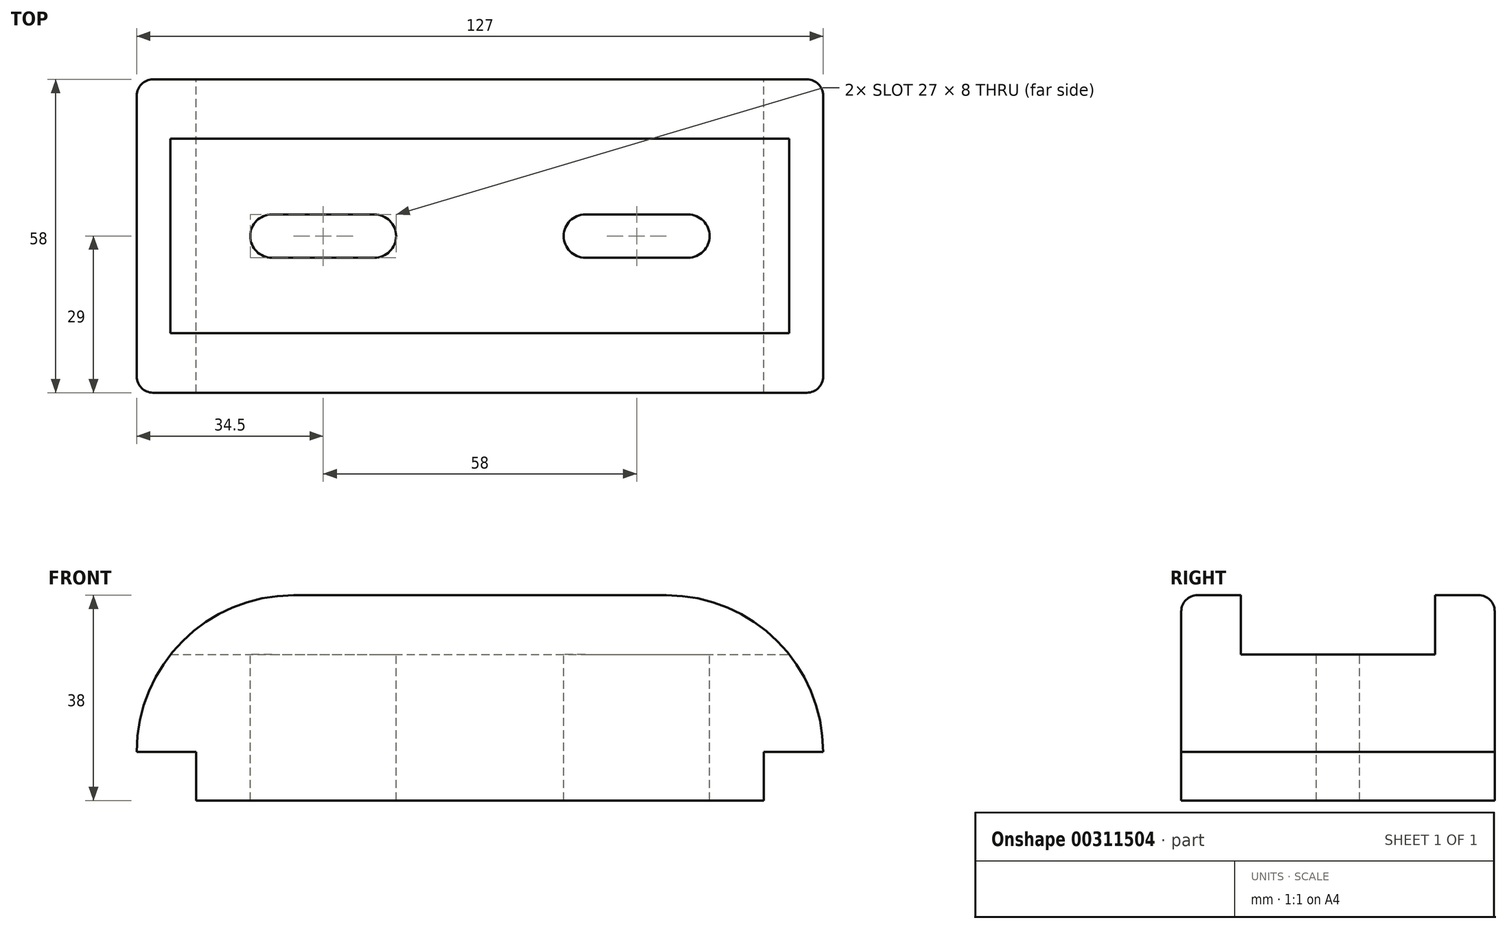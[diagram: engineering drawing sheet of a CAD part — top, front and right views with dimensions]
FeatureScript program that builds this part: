
annotation { "Feature Type Name" : "Feature", "Feature Type Description" : "" }
export const myFeature = defineFeature(function(context is Context, id is Id, definition is map)
    precondition{}
    {
        {
            var Q0;
            Q0=qCreatedBy(makeId("Front.planeOp"),FACE);
            var sketch = newSketch(context, id + "F0", { "sketchPlane" : qUnion([Q0])});
            skLineSegment(sketch, "E0", {"start": v(0, 0) * mm, "end": v(0, 9) * mm});
            skLineSegment(sketch, "E1", {"start": v(0, 9) * mm, "end": v(-11, 9) * mm});
            skLineSegment(sketch, "E2", {"start": v(0, 0) * mm, "end": v(105, 0) * mm});
            skLineSegment(sketch, "E3", {"start": v(105, 0) * mm, "end": v(105, 9) * mm});
            skLineSegment(sketch, "E4", {"start": v(105, 9) * mm, "end": v(116, 9) * mm});
            skLineSegment(sketch, "E5", {"start": v(18, 38) * mm, "end": v(87, 38) * mm});
            skArc(sketch, "E6", {"start": v(18, 38) * mm, "mid": v(-2.5, 29.5) * mm, "end": v(-11, 9) * mm});
            skArc(sketch, "E7", {"start": v(116, 9) * mm, "mid": v(107.5, 29.5) * mm, "end": v(87, 38) * mm});
            skSolve(sketch);
        }
        {
            var Q0;
            Q0 = qSketchRegion(id + "F0", true);
            extrude(context, id + "F1", {"entities" : qUnion([Q0]), "depth" : 58 * mm});
        }
        {
            var Q0;
            Q0=makeQuery(id+"F1.opExtrude","SWEPT_FACE",FACE,{"disambiguationData":[OSD([sQuery(id+"F0.wireOp",EDGE,"E5")])]});
            var sketch = newSketch(context, id + "F2", { "sketchPlane" : qUnion([Q0])});
            skLineSegment(sketch, "E8.bottom", {"start": v(-23.25, -11) * mm, "end": v(121.75, -11) * mm});
            skLineSegment(sketch, "E8.top", {"start": v(-23.25, -47) * mm, "end": v(121.75, -47) * mm});
            skLineSegment(sketch, "E8.left", {"start": v(-23.25, -11) * mm, "end": v(-23.25, -47) * mm});
            skLineSegment(sketch, "E8.right", {"start": v(121.75, -11) * mm, "end": v(121.75, -47) * mm});
            skSolve(sketch);
        }
        {
            var Q0;
            Q0 = qSketchRegion(id + "F2", true);
            extrude(context, id + "F3", {"entities" : qUnion([Q0]), "operationType" : NewBodyOperationType.REMOVE, "oppositeDirection" : true, "depth" : 11 * mm});
        }
        {
            var Q0;
            Q0=makeQuery(id+"F3.boolean.opBoolean","COPY",FACE,{"derivedFrom":makeQuery(id+"F3.opExtrude","CAP_FACE",FACE,{"disambiguationData":[OSD([sQuery(id+"F2.wireOp",EDGE,"E8.bottom"),sQuery(id+"F2.wireOp",EDGE,"E8.top"),sQuery(id+"F2.wireOp",EDGE,"E8.left"),sQuery(id+"F2.wireOp",EDGE,"E8.right")])],"isStart":false})});
            var sketch = newSketch(context, id + "F4", { "sketchPlane" : qUnion([Q0])});
            skArc(sketch, "E9", {"start": v(14, -25) * mm, "mid": v(10, -29) * mm, "end": v(14, -33) * mm});
            skArc(sketch, "E10", {"start": v(33, -33) * mm, "mid": v(37, -29) * mm, "end": v(33, -25) * mm});
            skLineSegment(sketch, "E11", {"start": v(14, -25) * mm, "end": v(33, -25) * mm});
            skLineSegment(sketch, "E12", {"start": v(14, -33) * mm, "end": v(33, -33) * mm});
            skArc(sketch, "E13", {"start": v(72, -25) * mm, "mid": v(68, -29) * mm, "end": v(72, -33) * mm});
            skArc(sketch, "E14", {"start": v(91, -33) * mm, "mid": v(95, -29) * mm, "end": v(91, -25) * mm});
            skLineSegment(sketch, "E15", {"start": v(72, -25) * mm, "end": v(91, -25) * mm});
            skLineSegment(sketch, "E16", {"start": v(72, -33) * mm, "end": v(91, -33) * mm});
            skSolve(sketch);
        }
        {
            var Q0;
            Q0 = qSketchRegion(id + "F4", true);
            extrude(context, id + "F5", {"entities" : qUnion([Q0]), "operationType" : NewBodyOperationType.REMOVE, "endBound" : BoundingType.THROUGH_ALL, "oppositeDirection" : true, "depth" : 25 * mm});
        }
        {
            var Q0;
            Q0=makeQuery(id+"F1.opExtrude","CAP_EDGE",EDGE,{"disambiguationData":[OSD([sQuery(id+"F0.wireOp",EDGE,"E5")])],"isStart":true});
            var Q1;
            Q1=makeQuery(id+"F1.opExtrude","CAP_EDGE",EDGE,{"disambiguationData":[OSD([sQuery(id+"F0.wireOp",EDGE,"E5")])],"isStart":false});
            fillet(context, id + "F6", {"entities" : qUnion([Q0, Q1]), "radius" : 3 * mm, "tangentPropagation" : true, "allowEdgeOverflow" : false});
        }
    });
